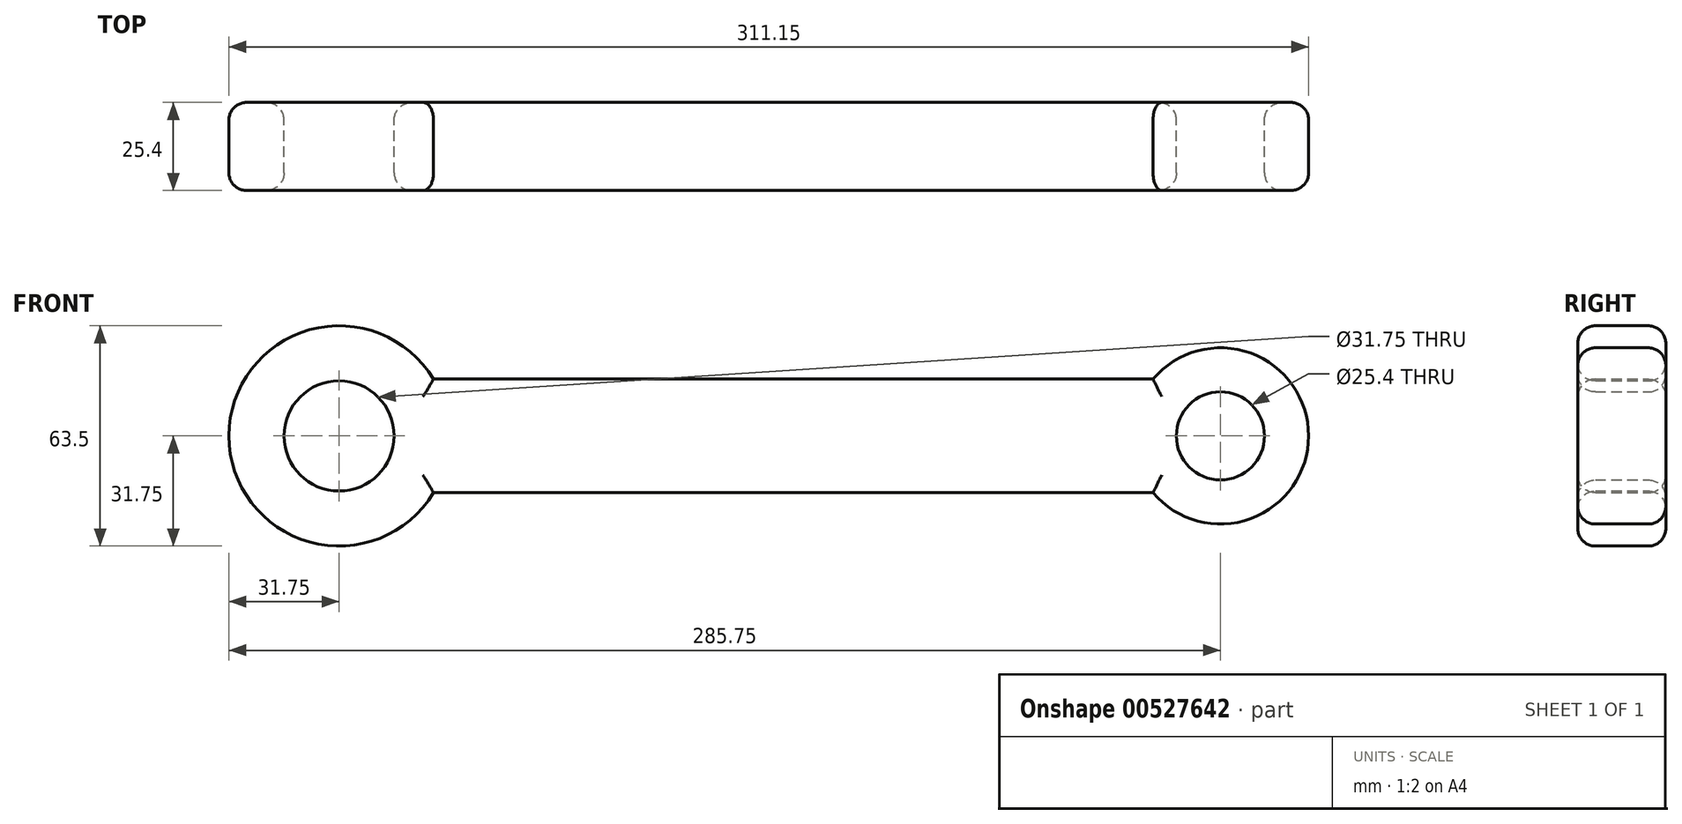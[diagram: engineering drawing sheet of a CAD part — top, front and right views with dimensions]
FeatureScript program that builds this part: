
annotation { "Feature Type Name" : "Feature", "Feature Type Description" : "" }
export const myFeature = defineFeature(function(context is Context, id is Id, definition is map)
    precondition{}
    {
        {
            var Q0;
            Q0=qCreatedBy(makeId("Front.planeOp"),FACE);
            var sketch = newSketch(context, id + "F0", { "sketchPlane" : qUnion([Q0])});
            skCircle(sketch, "E0", {"center": v(0, 0) * mm, "radius": 31.75 * mm});
            skCircle(sketch, "E1", {"center": v(254, 0) * mm, "radius": 25.4 * mm});
            skLineSegment(sketch, "E2", {"start": v(0, 0) * mm, "end": v(254, 0) * mm, "construction": true});
            skLineSegment(sketch, "E3", {"start": v(27.2, -16.37) * mm, "end": v(234.58, -16.37) * mm});
            skLineSegment(sketch, "E4.MirrorCS", {"start": v(27.2, 16.37) * mm, "end": v(234.58, 16.37) * mm});
            skCircle(sketch, "E5", {"center": v(0, 0) * mm, "radius": 15.88 * mm});
            skCircle(sketch, "E6", {"center": v(254, 0) * mm, "radius": 12.7 * mm});
            skSolve(sketch);
        }
        {
            var Q0;
            Q0 = qSketchRegion(id + "F0", true);
            extrude(context, id + "F1", {"entities" : qUnion([Q0]), "depth" : 25.4 * mm, "offsetDistance" : 25.4 * mm});
        }
        {
            var Q0;
            Q0=makeQuery(id+"F1.opExtrude","CAP_FACE",FACE,{"disambiguationData":[OSD([sQuery(id+"F0.wireOp",EDGE,"E0"),sQuery(id+"F0.wireOp",EDGE,"E1"),sQuery(id+"F0.wireOp",EDGE,"E3"),sQuery(id+"F0.wireOp",EDGE,"E4.MirrorCS"),sQuery(id+"F0.wireOp",EDGE,"E5"),sQuery(id+"F0.wireOp",EDGE,"E6")])],"isStart":false});
            fillet(context, id + "F2", {"entities" : qUnion([Q0]), "radius" : 5.08 * mm, "tangentPropagation" : true, "allowEdgeOverflow" : false});
        }
        {
            var Q0;
            Q0=makeQuery(id+"F1.opExtrude","CAP_FACE",FACE,{"disambiguationData":[OSD([sQuery(id+"F0.wireOp",EDGE,"E0"),sQuery(id+"F0.wireOp",EDGE,"E1"),sQuery(id+"F0.wireOp",EDGE,"E3"),sQuery(id+"F0.wireOp",EDGE,"E4.MirrorCS"),sQuery(id+"F0.wireOp",EDGE,"E5"),sQuery(id+"F0.wireOp",EDGE,"E6")])],"isStart":true});
            fillet(context, id + "F3", {"entities" : qUnion([Q0]), "radius" : 5.08 * mm, "tangentPropagation" : true, "allowEdgeOverflow" : false});
        }
    });
